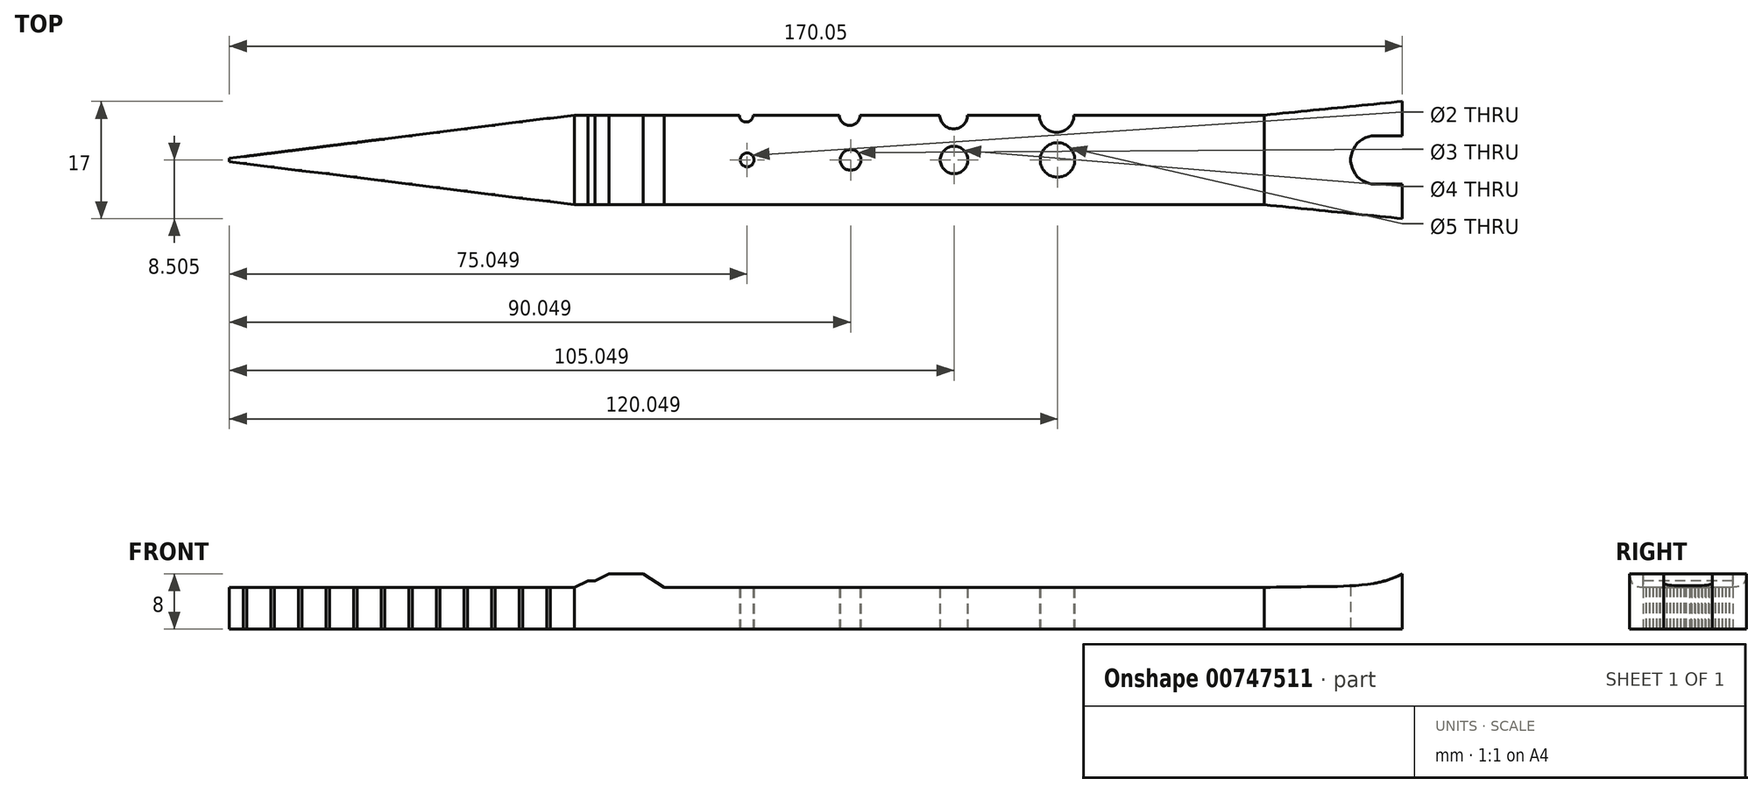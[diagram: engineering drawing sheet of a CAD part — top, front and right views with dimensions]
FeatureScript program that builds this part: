
annotation { "Feature Type Name" : "Feature", "Feature Type Description" : "" }
export const myFeature = defineFeature(function(context is Context, id is Id, definition is map)
    precondition{}
    {
        {
            var Q0;
            Q0=qCreatedBy(makeId("Top.planeOp"),FACE);
            var sketch = newSketch(context, id + "F0", { "sketchPlane" : qUnion([Q0])});
            skLineSegment(sketch, "E0", {"start": v(-52.12, -25.9) * mm, "end": v(47.93, -25.9) * mm});
            skLineSegment(sketch, "E1", {"start": v(47.93, -25.9) * mm, "end": v(47.93, -12.9) * mm});
            skLineSegment(sketch, "E2", {"start": v(47.93, -12.9) * mm, "end": v(20.3, -12.9) * mm});
            skCircle(sketch, "E3", {"center": v(-27.07, -19.4) * mm, "radius": 1 * mm});
            skCircle(sketch, "E4", {"center": v(-12.07, -19.4) * mm, "radius": 1.5 * mm});
            skCircle(sketch, "E5", {"center": v(2.93, -19.4) * mm, "radius": 2 * mm});
            skCircle(sketch, "E6", {"center": v(17.93, -19.4) * mm, "radius": 2.5 * mm});
            skArc(sketch, "E7", {"start": v(-28.2, -12.9) * mm, "mid": v(-27.2, -13.9) * mm, "end": v(-26.2, -12.9) * mm});
            skArc(sketch, "E8", {"start": v(-13.7, -12.9) * mm, "mid": v(-12.2, -14.4) * mm, "end": v(-10.7, -12.9) * mm});
            skArc(sketch, "E9", {"start": v(0.87, -12.9) * mm, "mid": v(2.87, -14.9) * mm, "end": v(4.87, -12.9) * mm});
            skArc(sketch, "E10", {"start": v(15.3, -12.9) * mm, "mid": v(17.8, -15.4) * mm, "end": v(20.3, -12.9) * mm});
            skLineSegment(sketch, "E11.trimOffspring", {"start": v(-28.2, -12.9) * mm, "end": v(-42.2, -12.9) * mm});
            skLineSegment(sketch, "E12.trimOffspring", {"start": v(-13.7, -12.9) * mm, "end": v(-26.2, -12.9) * mm});
            skLineSegment(sketch, "E13.trimOffspring", {"start": v(0.87, -12.9) * mm, "end": v(-10.7, -12.9) * mm});
            skLineSegment(sketch, "E14.trimOffspring", {"start": v(15.3, -12.9) * mm, "end": v(4.87, -12.9) * mm});
            skLineSegment(sketch, "E15", {"start": v(-42.2, -12.9) * mm, "end": v(-52.12, -12.9) * mm});
            skLineSegment(sketch, "E16", {"start": v(-42.2, -12.9) * mm, "end": v(-42.2, -25.9) * mm});
            skLineSegment(sketch, "E17", {"start": v(17.93, -19.4) * mm, "end": v(17.93, -25.9) * mm});
            skPoint(sketch, "E18.visualSharp", {"position": v(-102.16, -12.9) * mm});
            skPoint(sketch, "E19.visualSharp", {"position": v(-102.09, -25.9) * mm});
            skLineSegment(sketch, "E20", {"start": v(-102.12, -19.17) * mm, "end": v(-52.12, -12.9) * mm});
            skLineSegment(sketch, "E21", {"start": v(-52.12, -12.9) * mm, "end": v(-52.12, -25.9) * mm});
            skLineSegment(sketch, "E22", {"start": v(-52.12, -25.9) * mm, "end": v(-102.12, -19.67) * mm});
            skLineSegment(sketch, "E23", {"start": v(-102.12, -19.17) * mm, "end": v(-102.12, -19.67) * mm});
            skSolve(sketch);
        }
        {
            var Q0;
            {var subQ3=sQuery(id+"F0.wireOp",EDGE,"E1");Q0=makeQuery(id+"F0.imprint","IMPRINT",FACE,{"disambiguationData":[TD([[makeQuery(id+"F0.imprint","IMPRINT",EDGE,{"derivedFrom":subQ3}),1.0]])]});}
            var Q1;
            Q1=makeQuery(id+"F0.imprint","IMPRINT",FACE,{"disambiguationData":[TD([[makeQuery(id+"F0.imprint","IMPRINT",EDGE,{"derivedFrom":sQuery(id+"F0.wireOp",EDGE,"E15")}),1.0]])]});
            var Q2;
            Q2=qSketchRegion(id+"F2",true);
            var Q3;
            Q3=makeQuery(id+"F0.imprint","IMPRINT",FACE,{"disambiguationData":[TD([[makeQuery(id+"F0.imprint","IMPRINT",EDGE,{"derivedFrom":sQuery(id+"F0.wireOp",EDGE,"E20")}),-1.0]])]});
            extrude(context, id + "F1", {"entities" : qUnion([Q0, Q1, Q2, Q3]), "depth" : 6 * mm, "offsetDistance" : 25 * mm});
        }
        {
            var Q0;
            Q0=makeQuery(id+"F1.opExtrude","CAP_FACE",FACE,{"disambiguationData":[OSD([sQuery(id+"F0.wireOp",EDGE,"uh8EjRIv-oyds-LonH-DEWT-FKtuM7sv1xbY"),sQuery(id+"F0.wireOp",EDGE,"2pE5EAkt-IuKl-0Sab-UQfI-aqEs6KhZttEm"),sQuery(id+"F0.wireOp",EDGE,"Nk6HZn5N-y9iB-Nk6B-fPmU-OZDAcxOevotu"),sQuery(id+"F0.wireOp",EDGE,"LXX49E4n-5PRi-B9FO-bH7N-pa6ycjuBgqBC"),sQuery(id+"F0.wireOp",EDGE,"53KMTElE-K7W9-ORrf-RCAp-qNT4eaaVkteF"),sQuery(id+"F0.wireOp",EDGE,"P7PF4Mbg-ef0C-n9oX-XZ09-ZLFXLgH8y7fW"),sQuery(id+"F0.wireOp",EDGE,"su197C0L-hHtV-Jca1-MSLm-PElzWjnIUR3Y"),sQuery(id+"F0.wireOp",EDGE,"EV9Pacv8-165I-bCM3-OcYT-9LR3dg5SSEyu"),sQuery(id+"F0.wireOp",EDGE,"19IYVO1Q-Y4kt-bx1a-DxFm-OXG8GlXLaGFM"),sQuery(id+"F0.wireOp",EDGE,"65VxX6mh-rfcX-KxfM-GORW-ms9ADtBnMzlR"),sQuery(id+"F0.wireOp",EDGE,"7bQUvBXv-wM8X-eBwg-Mk0h-ePabGQXhmWVm"),sQuery(id+"F0.wireOp",EDGE,"bDx1VqJG-FhMZ-ysIe-255i-NBJnI1b9v1Xd"),sQuery(id+"F0.wireOp",EDGE,"GWuhjFGg-mN8e-GpBZ-US7o-J5IPN2826qVD"),sQuery(id+"F0.wireOp",EDGE,"91LzrW2M-BcOK-ah0N-KhqT-TaDJfhBesgPh"),sQuery(id+"F0.wireOp",EDGE,"1k80qitz-qzns-NigU-Vkyj-1TzsJOIY6Jo9"),sQuery(id+"F0.wireOp",EDGE,"p5sEo6Ta-pkgy-Fa4L-bMfm-GfEhippCeM6v"),sQuery(id+"F0.wireOp",EDGE,"VcT0GBPq-V1kq-JeiP-DT5O-q3OzsVNUBB7H"),sQuery(id+"F0.wireOp",EDGE,"vWu1ZsAQ-pDto-N3AH-TT21-yHdSeIgjR8fg"),sQuery(id+"F0.wireOp",EDGE,"vBJXVKXv-qYgn-2ukd-IsI3-EiIpIBPK8Vaz"),sQuery(id+"F0.wireOp",EDGE,"G37NeImH-WY8i-Es2l-a97g-44kHUUvCxSSy"),sQuery(id+"F0.wireOp",EDGE,"E7LrDzYy-OpsH-mPZP-qLcD-qzzZRt0giBqK"),sQuery(id+"F0.wireOp",EDGE,"s3JVjWtr-fkdu-SgC5-uSSM-x588ayeuHTqY"),sQuery(id+"F0.wireOp",EDGE,"Z1yXTLh1-1L1P-RAfO-bNF2-wSMogvR3wL57"),sQuery(id+"F0.wireOp",EDGE,"ZUVO2fO2-Q0JX-bRAt-EWbK-FMEUTOadSTGL"),sQuery(id+"F0.wireOp",EDGE,"OpzXb7L7-065u-pUx9-msa7-Or2I1k12Jhel"),sQuery(id+"F0.wireOp",EDGE,"E0"),sQuery(id+"F0.wireOp",EDGE,"E1"),sQuery(id+"F0.wireOp",EDGE,"E2"),sQuery(id+"F0.wireOp",EDGE,"E3"),sQuery(id+"F0.wireOp",EDGE,"E4"),sQuery(id+"F0.wireOp",EDGE,"E5"),sQuery(id+"F0.wireOp",EDGE,"E6"),sQuery(id+"F0.wireOp",EDGE,"E7"),sQuery(id+"F0.wireOp",EDGE,"E8"),sQuery(id+"F0.wireOp",EDGE,"E9"),sQuery(id+"F0.wireOp",EDGE,"E10"),sQuery(id+"F0.wireOp",EDGE,"E11.trimOffspring"),sQuery(id+"F0.wireOp",EDGE,"E12.trimOffspring"),sQuery(id+"F0.wireOp",EDGE,"E13.trimOffspring"),sQuery(id+"F0.wireOp",EDGE,"E14.trimOffspring")])],"isStart":true});
            var sketch = newSketch(context, id + "F2", { "sketchPlane" : qUnion([Q0])});
            skLineSegment(sketch, "E24", {"start": v(47.93, 12.9) * mm, "end": v(47.93, 25.9) * mm});
            skLineSegment(sketch, "E25", {"start": v(47.93, 25.9) * mm, "end": v(67.93, 27.9) * mm});
            skLineSegment(sketch, "E26", {"start": v(47.93, 12.9) * mm, "end": v(67.93, 10.9) * mm});
            skLineSegment(sketch, "E27", {"start": v(67.93, 27.9) * mm, "end": v(67.93, 22.9) * mm});
            skLineSegment(sketch, "E28", {"start": v(67.93, 10.9) * mm, "end": v(67.93, 15.9) * mm});
            skLineSegment(sketch, "E29", {"start": v(67.93, 15.9) * mm, "end": v(63.93, 15.9) * mm});
            skLineSegment(sketch, "E30", {"start": v(67.93, 22.9) * mm, "end": v(63.93, 22.9) * mm});
            skArc(sketch, "E31", {"start": v(63.93, 15.9) * mm, "mid": v(60.43, 19.4) * mm, "end": v(63.93, 22.9) * mm});
            skSolve(sketch);
        }
        {
            var Q0;
            Q0=makeQuery(id+"F2.imprint","IMPRINT",FACE,{"disambiguationData":[TD([[makeQuery(id+"F2.imprint","IMPRINT",EDGE,{"derivedFrom":sQuery(id+"F2.wireOp",EDGE,"E24")}),1.0]])]});
            extrude(context, id + "F3", {"entities" : qUnion([Q0]), "operationType" : NewBodyOperationType.ADD, "oppositeDirection" : true, "depth" : 8 * mm, "offsetDistance" : 25 * mm});
        }
        {
            var Q0;
            Q0=makeQuery(id+"F1.opExtrude","SWEPT_FACE",FACE,{"disambiguationData":[OSD([sQuery(id+"F0.wireOp",EDGE,"E0")])]});
            var sketch = newSketch(context, id + "F4", { "sketchPlane" : qUnion([Q0])});
            skFitSpline(sketch, "E32", {"points": [v(47.93, 6) * mm, v(67.93, 8) * mm, v(72.49, 16.65) * mm], "startDerivative": vector(42.2, 1.96) * mm, "endDerivative": vector(-1.7, 25.64) * mm});
            skLineSegment(sketch, "E33", {"start": v(47.93, 21.53) * mm, "end": v(72.53, 21.53) * mm});
            skLineSegment(sketch, "E34", {"start": v(72.53, 21.53) * mm, "end": v(72.53, -3.93) * mm});
            skLineSegment(sketch, "E35", {"start": v(72.53, -3.93) * mm, "end": v(47.93, -3.93) * mm});
            skLineSegment(sketch, "E36", {"start": v(47.93, -3.93) * mm, "end": v(47.93, 0) * mm});
            skLineSegment(sketch, "E37", {"start": v(47.93, 6) * mm, "end": v(46.54, 6) * mm});
            skLineSegment(sketch, "E38", {"start": v(46.54, 6) * mm, "end": v(46.54, 21.53) * mm});
            skLineSegment(sketch, "E39", {"start": v(46.54, 21.53) * mm, "end": v(47.93, 21.53) * mm});
            skLineSegment(sketch, "E40", {"start": v(67.93, 8) * mm, "end": v(67.93, 7.24) * mm});
            skFitSpline(sketch, "E41", {"points": [v(47.93, 0) * mm, v(67.93, 7.24) * mm, v(72.77, 16.03) * mm, v(78.73, 9.87) * mm], "startDerivative": vector(59.64, 6.8) * mm, "endDerivative": vector(27.46, -36.02) * mm});
            skSolve(sketch);
        }
        {
            var Q0;
            Q0=makeQuery(id+"F4.imprint","IMPRINT",FACE,{"disambiguationData":[TD([[makeQuery(id+"F4.imprint","IMPRINT",EDGE,{"derivedFrom":sQuery(id+"F4.wireOp",EDGE,"E33")}),-1.0]])]});
            var Q1;
            {var subQ1=sQuery(id+"F2.wireOp",EDGE,"E25");var subQ2=makeQuery(id+"F3.opExtrude","CAP_EDGE",EDGE,{"disambiguationData":[OSD([subQ1])],"isStart":false});Q1=makeQuery(id+"F4.imprint","IMPRINT",FACE,{"disambiguationData":[TD([[makeQuery(id+"F4.imprint","IMPRINT",EDGE,{"derivedFrom":subQ2}),-1.0]])]});}
            var Q2;
            {var subQ1=sQuery(id+"F2.wireOp",EDGE,"E25");var subQ3=makeQuery(id+"F3.opExtrude","CAP_EDGE",EDGE,{"disambiguationData":[OSD([subQ1])],"isStart":true});Q2=makeQuery(id+"F4.imprint","IMPRINT",FACE,{"disambiguationData":[TD([[makeQuery(id+"F4.imprint","IMPRINT",EDGE,{"derivedFrom":subQ3}),1.0]])]});}
            extrude(context, id + "F5", {"entities" : qUnion([Q0, Q1, Q2]), "operationType" : NewBodyOperationType.REMOVE, "oppositeDirection" : true, "depth" : 25 * mm, "offsetDistance" : 25 * mm, "hasSecondDirection" : true, "secondDirectionOppositeDirection" : false, "secondDirectionDepth" : 25 * mm});
        }
        {
            var Q0;
            {var subQ0=sQuery(id+"F0.wireOp",EDGE,"E10");var subQ1=sQuery(id+"F0.wireOp",EDGE,"E8");var subQ2=sQuery(id+"F0.wireOp",EDGE,"E7");var subQ3=sQuery(id+"F0.wireOp",EDGE,"E6");var subQ11=sQuery(id+"F0.wireOp",EDGE,"E5");var subQ12=sQuery(id+"F0.wireOp",EDGE,"E9");var subQ13=sQuery(id+"F0.wireOp",EDGE,"E0");var subQ14=sQuery(id+"F0.wireOp",EDGE,"E3");var subQ15=sQuery(id+"F0.wireOp",EDGE,"E2");var subQ16=sQuery(id+"F0.wireOp",EDGE,"E4");var subQ17=sQuery(id+"F0.wireOp",EDGE,"E15");var subQ18=sQuery(id+"F0.wireOp",EDGE,"E11.trimOffspring");var subQ19=sQuery(id+"F0.wireOp",EDGE,"E12.trimOffspring");var subQ20=sQuery(id+"F0.wireOp",EDGE,"E13.trimOffspring");var subQ21=sQuery(id+"F0.wireOp",EDGE,"E14.trimOffspring");Q0=makeQuery(id+"F9.boolean.opBoolean","SPLIT",FACE,{"disambiguationData":[TD([makeQuery(id+"F1.opExtrude","SWEPT_FACE",FACE,{"disambiguationData":[OSD([subQ15])]})])],"derivedFrom":makeQuery(id+"F1.opExtrude","CAP_FACE",FACE,{"disambiguationData":[OSD([subQ13,sQuery(id+"F0.wireOp",EDGE,"E1"),subQ15,subQ14,subQ16,subQ11,subQ3,subQ2,subQ1,subQ12,subQ0,subQ18,subQ19,subQ20,subQ21,subQ17,sQuery(id+"F0.wireOp",EDGE,"E20"),sQuery(id+"F0.wireOp",EDGE,"E22"),sQuery(id+"F0.wireOp",EDGE,"E23")])],"isStart":false})});}
            var sketch = newSketch(context, id + "F6", { "sketchPlane" : qUnion([Q0])});
            skLineSegment(sketch, "E42", {"start": v(-39.12, -25.9) * mm, "end": v(-52.12, -25.9) * mm, "construction": true});
            skLineSegment(sketch, "E43", {"start": v(-102.12, -19.4) * mm, "end": v(-102.12, -19.15) * mm});
            skLineSegment(sketch, "E44", {"start": v(-52.12, -12.9) * mm, "end": v(-55.62, -13.33) * mm});
            skLineSegment(sketch, "E45", {"start": v(-100.12, -18.9) * mm, "end": v(-99.62, -18.9) * mm});
            skLineSegment(sketch, "E46", {"start": v(-99.62, -18.9) * mm, "end": v(-99.62, -18.83) * mm});
            skLineSegment(sketch, "E47", {"start": v(-96.12, -18.4) * mm, "end": v(-95.62, -18.4) * mm});
            skLineSegment(sketch, "E48", {"start": v(-95.62, -18.4) * mm, "end": v(-95.62, -18.33) * mm});
            skLineSegment(sketch, "E49", {"start": v(-92.12, -17.9) * mm, "end": v(-91.62, -17.9) * mm});
            skLineSegment(sketch, "E50", {"start": v(-91.62, -17.9) * mm, "end": v(-91.62, -17.83) * mm});
            skLineSegment(sketch, "E51", {"start": v(-88.12, -17.4) * mm, "end": v(-87.62, -17.4) * mm});
            skLineSegment(sketch, "E52", {"start": v(-87.62, -17.4) * mm, "end": v(-87.62, -17.33) * mm});
            skLineSegment(sketch, "E53", {"start": v(-84.12, -16.9) * mm, "end": v(-83.62, -16.9) * mm});
            skLineSegment(sketch, "E54", {"start": v(-83.62, -16.9) * mm, "end": v(-83.62, -16.83) * mm});
            skLineSegment(sketch, "E55", {"start": v(-80.12, -16.4) * mm, "end": v(-79.62, -16.4) * mm});
            skLineSegment(sketch, "E56", {"start": v(-79.62, -16.4) * mm, "end": v(-79.62, -16.33) * mm});
            skLineSegment(sketch, "E57", {"start": v(-76.12, -15.9) * mm, "end": v(-75.62, -15.9) * mm});
            skLineSegment(sketch, "E58", {"start": v(-75.62, -15.9) * mm, "end": v(-75.62, -15.83) * mm});
            skLineSegment(sketch, "E59", {"start": v(-72.12, -15.4) * mm, "end": v(-71.62, -15.4) * mm});
            skLineSegment(sketch, "E60", {"start": v(-71.62, -15.4) * mm, "end": v(-71.62, -15.33) * mm});
            skLineSegment(sketch, "E61", {"start": v(-68.12, -14.9) * mm, "end": v(-67.62, -14.9) * mm});
            skLineSegment(sketch, "E62", {"start": v(-67.62, -14.9) * mm, "end": v(-67.62, -14.83) * mm});
            skLineSegment(sketch, "E63", {"start": v(-64.12, -14.4) * mm, "end": v(-63.62, -14.4) * mm});
            skLineSegment(sketch, "E64", {"start": v(-63.62, -14.4) * mm, "end": v(-63.62, -14.33) * mm});
            skLineSegment(sketch, "E65", {"start": v(-60.12, -13.9) * mm, "end": v(-59.62, -13.9) * mm});
            skLineSegment(sketch, "E66", {"start": v(-59.62, -13.9) * mm, "end": v(-59.62, -13.83) * mm});
            skLineSegment(sketch, "E67", {"start": v(-56.12, -13.4) * mm, "end": v(-55.62, -13.4) * mm});
            skLineSegment(sketch, "E68", {"start": v(-55.62, -13.4) * mm, "end": v(-55.62, -13.33) * mm});
            skLineSegment(sketch, "E69.trimOffspring", {"start": v(-56.12, -13.4) * mm, "end": v(-59.62, -13.83) * mm});
            skLineSegment(sketch, "E70.trimOffspring", {"start": v(-60.12, -13.9) * mm, "end": v(-63.62, -14.33) * mm});
            skLineSegment(sketch, "E71.trimOffspring", {"start": v(-64.12, -14.4) * mm, "end": v(-67.62, -14.83) * mm});
            skLineSegment(sketch, "E72.trimOffspring", {"start": v(-68.12, -14.9) * mm, "end": v(-71.62, -15.33) * mm});
            skLineSegment(sketch, "E73.trimOffspring", {"start": v(-72.12, -15.4) * mm, "end": v(-75.62, -15.83) * mm});
            skLineSegment(sketch, "E74.trimOffspring", {"start": v(-76.12, -15.9) * mm, "end": v(-79.62, -16.33) * mm});
            skLineSegment(sketch, "E75.trimOffspring", {"start": v(-80.12, -16.4) * mm, "end": v(-83.62, -16.83) * mm});
            skLineSegment(sketch, "E76.trimOffspring", {"start": v(-84.12, -16.9) * mm, "end": v(-87.62, -17.33) * mm});
            skLineSegment(sketch, "E77.trimOffspring", {"start": v(-88.12, -17.4) * mm, "end": v(-91.62, -17.83) * mm});
            skLineSegment(sketch, "E78.trimOffspring", {"start": v(-92.12, -17.9) * mm, "end": v(-95.62, -18.33) * mm});
            skLineSegment(sketch, "E79.trimOffspring", {"start": v(-96.12, -18.4) * mm, "end": v(-99.62, -18.83) * mm});
            skLineSegment(sketch, "E80.trimOffspring", {"start": v(-100.12, -18.9) * mm, "end": v(-102.12, -19.15) * mm});
            skLineSegment(sketch, "E81.MirrorCS", {"start": v(-59.62, -24.9) * mm, "end": v(-59.62, -24.96) * mm});
            skLineSegment(sketch, "E82.MirrorCS", {"start": v(-60.12, -24.9) * mm, "end": v(-59.62, -24.9) * mm});
            skLineSegment(sketch, "E83.MirrorCS", {"start": v(-88.12, -21.4) * mm, "end": v(-87.62, -21.4) * mm});
            skLineSegment(sketch, "E84.MirrorCS", {"start": v(-75.62, -22.9) * mm, "end": v(-75.62, -22.96) * mm});
            skLineSegment(sketch, "E85.MirrorCS", {"start": v(-55.62, -25.4) * mm, "end": v(-55.62, -25.46) * mm});
            skLineSegment(sketch, "E86.MirrorCS", {"start": v(-71.62, -23.4) * mm, "end": v(-71.62, -23.46) * mm});
            skLineSegment(sketch, "E87.MirrorCS", {"start": v(-68.12, -23.9) * mm, "end": v(-67.62, -23.9) * mm});
            skLineSegment(sketch, "E88.MirrorCS", {"start": v(-83.62, -21.9) * mm, "end": v(-83.62, -21.96) * mm});
            skLineSegment(sketch, "E89.MirrorCS", {"start": v(-99.62, -19.9) * mm, "end": v(-99.62, -19.96) * mm});
            skLineSegment(sketch, "E90.MirrorCS", {"start": v(-100.12, -19.9) * mm, "end": v(-99.62, -19.9) * mm});
            skLineSegment(sketch, "E91.MirrorCS", {"start": v(-95.62, -20.4) * mm, "end": v(-95.62, -20.46) * mm});
            skLineSegment(sketch, "E92.MirrorCS", {"start": v(-84.12, -21.9) * mm, "end": v(-83.62, -21.9) * mm});
            skLineSegment(sketch, "E93.MirrorCS", {"start": v(-72.12, -23.4) * mm, "end": v(-71.62, -23.4) * mm});
            skLineSegment(sketch, "E94.MirrorCS", {"start": v(-63.62, -24.4) * mm, "end": v(-63.62, -24.46) * mm});
            skLineSegment(sketch, "E95.MirrorCS", {"start": v(-87.62, -21.4) * mm, "end": v(-87.62, -21.46) * mm});
            skLineSegment(sketch, "E96.MirrorCS", {"start": v(-56.12, -25.4) * mm, "end": v(-55.62, -25.4) * mm});
            skLineSegment(sketch, "E97.MirrorCS", {"start": v(-64.12, -24.4) * mm, "end": v(-63.62, -24.4) * mm});
            skLineSegment(sketch, "E98.MirrorCS", {"start": v(-96.12, -20.4) * mm, "end": v(-95.62, -20.4) * mm});
            skLineSegment(sketch, "E99.MirrorCS", {"start": v(-67.62, -23.9) * mm, "end": v(-67.62, -23.96) * mm});
            skLineSegment(sketch, "E100.MirrorCS", {"start": v(-76.12, -22.9) * mm, "end": v(-75.62, -22.9) * mm});
            skLineSegment(sketch, "E101.MirrorCS", {"start": v(-91.62, -20.9) * mm, "end": v(-91.62, -20.96) * mm});
            skLineSegment(sketch, "E102.MirrorCS", {"start": v(-80.12, -22.4) * mm, "end": v(-79.62, -22.4) * mm});
            skLineSegment(sketch, "E103.MirrorCS", {"start": v(-79.62, -22.4) * mm, "end": v(-79.62, -22.46) * mm});
            skLineSegment(sketch, "E104.MirrorCS", {"start": v(-92.12, -20.9) * mm, "end": v(-91.62, -20.9) * mm});
            skLineSegment(sketch, "E105.MirrorCS", {"start": v(-80.12, -22.4) * mm, "end": v(-83.62, -21.96) * mm});
            skLineSegment(sketch, "E106.MirrorCS", {"start": v(-84.12, -21.9) * mm, "end": v(-87.62, -21.46) * mm});
            skLineSegment(sketch, "E107.MirrorCS", {"start": v(-52.12, -25.9) * mm, "end": v(-55.62, -25.46) * mm});
            skLineSegment(sketch, "E108.MirrorCS", {"start": v(-64.12, -24.4) * mm, "end": v(-67.62, -23.96) * mm});
            skLineSegment(sketch, "E109.MirrorCS", {"start": v(-68.12, -23.9) * mm, "end": v(-71.62, -23.46) * mm});
            skLineSegment(sketch, "E110.MirrorCS", {"start": v(-72.12, -23.4) * mm, "end": v(-75.62, -22.96) * mm});
            skLineSegment(sketch, "E111.MirrorCS", {"start": v(-56.12, -25.4) * mm, "end": v(-59.62, -24.96) * mm});
            skLineSegment(sketch, "E112.MirrorCS", {"start": v(-76.12, -22.9) * mm, "end": v(-79.62, -22.46) * mm});
            skLineSegment(sketch, "E113.MirrorCS", {"start": v(-88.12, -21.4) * mm, "end": v(-91.62, -20.96) * mm});
            skLineSegment(sketch, "E114.MirrorCS", {"start": v(-96.12, -20.4) * mm, "end": v(-99.62, -19.96) * mm});
            skLineSegment(sketch, "E115.MirrorCS", {"start": v(-60.12, -24.9) * mm, "end": v(-63.62, -24.46) * mm});
            skLineSegment(sketch, "E116.MirrorCS", {"start": v(-100.12, -19.9) * mm, "end": v(-102.12, -19.65) * mm});
            skLineSegment(sketch, "E117.MirrorCS", {"start": v(-92.12, -20.9) * mm, "end": v(-95.62, -20.46) * mm});
            skLineSegment(sketch, "E118", {"start": v(-52.12, -12.9) * mm, "end": v(-54.34, -8.3) * mm});
            skLineSegment(sketch, "E119", {"start": v(-54.34, -8.3) * mm, "end": v(-108.26, -12.9) * mm});
            skLineSegment(sketch, "E120", {"start": v(-108.26, -12.9) * mm, "end": v(-106.08, -29.54) * mm});
            skLineSegment(sketch, "E121", {"start": v(-52.12, -25.9) * mm, "end": v(-62.2, -31.86) * mm});
            skLineSegment(sketch, "E122", {"start": v(-62.2, -31.86) * mm, "end": v(-106.08, -29.54) * mm});
            skLineSegment(sketch, "E123", {"start": v(-102.12, -19.4) * mm, "end": v(-102.12, -19.65) * mm});
            skSolve(sketch);
        }
        {
            var Q0;
            Q0 = qSketchRegion(id + "F6", true);
            extrude(context, id + "F7", {"entities" : qUnion([Q0]), "operationType" : NewBodyOperationType.REMOVE, "oppositeDirection" : true, "depth" : 25 * mm, "offsetDistance" : 25 * mm});
        }
        {
            var Q0;
            Q0=makeQuery(id+"F1.opExtrude","SWEPT_FACE",FACE,{"disambiguationData":[OSD([sQuery(id+"F0.wireOp",EDGE,"E0")])]});
            var sketch = newSketch(context, id + "F8", { "sketchPlane" : qUnion([Q0])});
            skLineSegment(sketch, "E124", {"start": v(-52.12, 6) * mm, "end": v(-50.12, 6) * mm});
            skLineSegment(sketch, "E125", {"start": v(-50.12, 7) * mm, "end": v(-49.12, 7) * mm});
            skLineSegment(sketch, "E126", {"start": v(-39.12, 6) * mm, "end": v(-50.12, 6) * mm});
            skLineSegment(sketch, "E127", {"start": v(-52.12, 6) * mm, "end": v(-50.12, 7) * mm});
            skLineSegment(sketch, "E128", {"start": v(-49.12, 7) * mm, "end": v(-47.12, 7) * mm, "construction": true});
            skLineSegment(sketch, "E129", {"start": v(-47.12, 7) * mm, "end": v(-47.12, 8) * mm, "construction": true});
            skLineSegment(sketch, "E130", {"start": v(-49.12, 7) * mm, "end": v(-47.12, 8) * mm});
            skLineSegment(sketch, "E131", {"start": v(-47.12, 8) * mm, "end": v(-42.12, 8) * mm});
            skLineSegment(sketch, "E132", {"start": v(-42.12, 8) * mm, "end": v(-39.12, 6) * mm});
            skSolve(sketch);
        }
        {
            var Q0;
            Q0=makeQuery(id+"F8.imprint","IMPRINT",FACE,{"disambiguationData":[TD([[makeQuery(id+"F8.imprint","IMPRINT",EDGE,{"derivedFrom":sQuery(id+"F8.wireOp",EDGE,"E124")}),1.0]])]});
            extrude(context, id + "F9", {"entities" : qUnion([Q0]), "operationType" : NewBodyOperationType.ADD, "oppositeDirection" : true, "depth" : 13 * mm, "offsetDistance" : 25 * mm});
        }
    });
